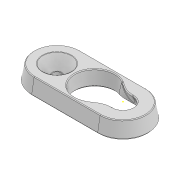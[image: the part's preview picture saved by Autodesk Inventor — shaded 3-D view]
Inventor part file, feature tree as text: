
AUTODESK INVENTOR PART (.ipt)
format: ipt  version: 2021 (Build 250183000, 183)  size: 354,816 bytes
history: native  units: mm
features: sketch x7, extrude x5, projected_geometry x5, fillet x4, draft x3, chamfer x2, hole x1
ambient origin geometry x8: Origin, YZ Plane, XZ Plane, XY Plane, X Axis, Y Axis, Z Axis, Center Point
bodies: Body1 (feature_tree)
feature tree (27):
  extrude  "Extrusion11"  Depth=9.0mm TaperAngle=0.0deg
  extrude  "Extrusion12"  Depth=18.0mm TaperAngle=0.0deg
  hole  "Hole2"  [1 undecoded]
  sketch  "Sketch19"  dims[d76=29.0mm d77=42.0mm]
  draft  "FaceDraft1"
  sketch  "Sketch20"  dims[d78=1.0mm d79=0.0mm d80=1.0mm d81=0.0mm d82=25.0mm d83=15.0mm d84=1.745329mm d85=0.174533mm]
  extrude  "Extrusion13"  Depth=42.0mm
  extrude  "Extrusion14"  Depth=1.0mm TaperAngle=0.0deg
  fillet  "Fillet1"  Radius=25.0mm
  draft  "FaceDraft2"
  draft  "FaceDraft3"
  fillet  "Fillet2"  Radius=15.0mm
  fillet  "Fillet3"  Radius=1.745329mm
  fillet  "Fillet4"  Radius=0.174533mm
  chamfer  "Chamfer1"  Distance=0.5mm
  extrude  "Extrusion15"  Depth=1.0mm TaperAngle=45.0deg
  chamfer  "Chamfer2"  Distance=82.75mm
  sketch  "Sketch16"  dims[d61=29.0mm d62=9.0mm d63=0.0mm]
  sketch  "Sketch17"  dims[d65=18.0mm d66=26.0mm d67=0.0mm]
  projected_geometry  "Projected Loop17"
  sketch  "Sketch18"  dims[d68=5.5mm d69=6.0mm d70=18.15mm d71=2.0mm d72=90.0deg d73=37.0mm d74=20.594885mm d75=-5.235988mm]
  projected_geometry  "Projected Loop18"
  projected_geometry  "Projected Loop19"
  sketch  "Sketch21"  dims[d86=0.5mm]
  projected_geometry  "Projected Loop20"
  sketch  "Sketch22"  dims[d87=0.5mm d88=0.5mm d89=1.0mm d90=2.0mm d91=45.0deg d92=82.75mm d93=0.0mm d94=0.95mm d95=2.0mm d96=45.0deg d97=6.0mm d98=1.0mm d99=1.0mm d100=0.15mm d101=0.25mm d102=0.375mm d103=14.3117mm d104=0.75mm d105=20.594885mm d106=0.0625mm d107=0.75mm d108=0.375mm]
  projected_geometry  "Projected Loop21"
note: 1 required parameter value undecoded (feature->parameter linkage not recoverable at this tier; creation-order binding heuristic only, values carry confidence <= 0.55)
